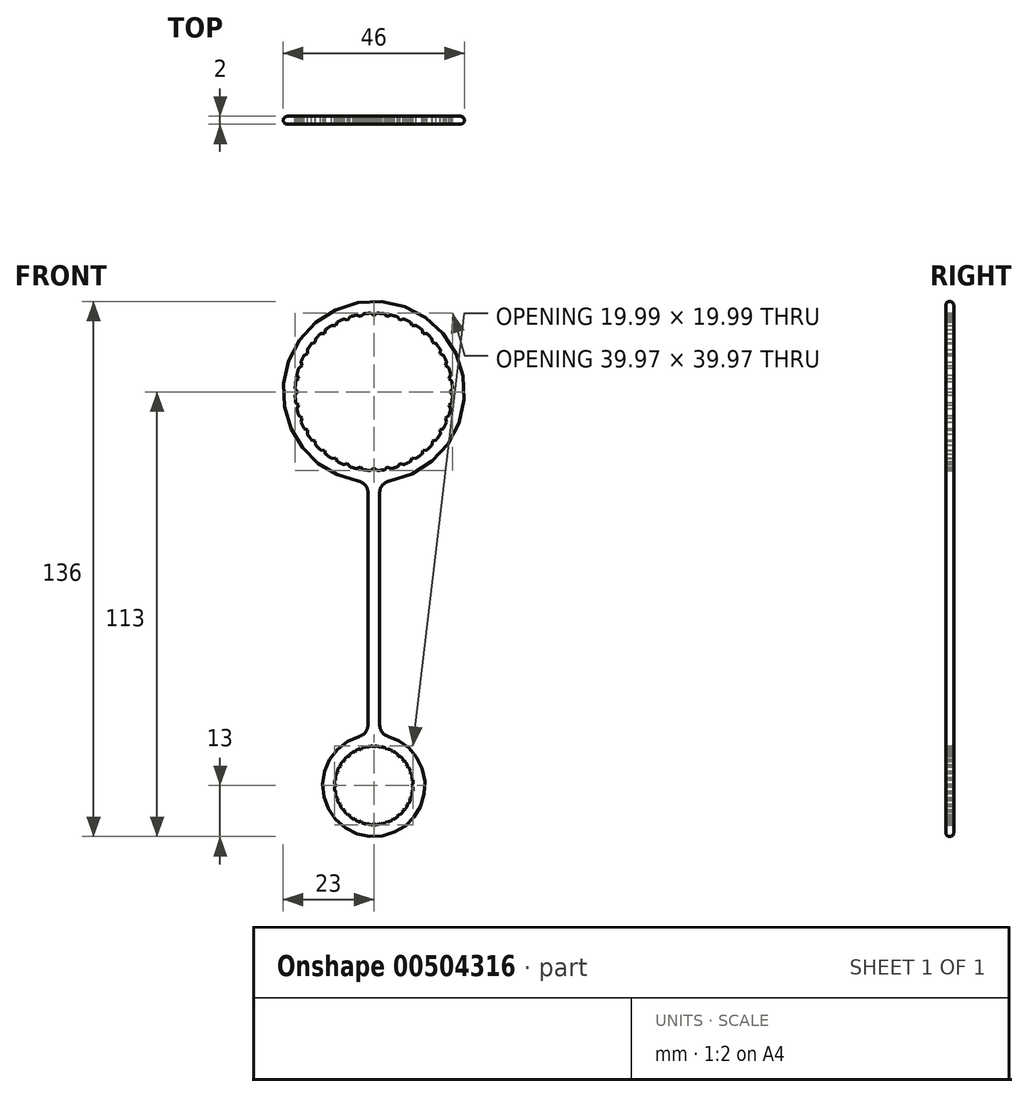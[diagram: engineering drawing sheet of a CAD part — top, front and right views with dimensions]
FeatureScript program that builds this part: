
annotation { "Feature Type Name" : "Feature", "Feature Type Description" : "" }
export const myFeature = defineFeature(function(context is Context, id is Id, definition is map)
    precondition{}
    {
        {
            var Q0;
            Q0=qCreatedBy(makeId("Front.planeOp"),FACE);
            var sketch = newSketch(context, id + "F0", { "sketchPlane" : qUnion([Q0])});
            skArc(sketch, "E0", {"start": v(6.06, 19.06) * mm, "mid": v(5.18, 19.32) * mm, "end": v(4.28, 19.54) * mm});
            skArc(sketch, "E1", {"start": v(-0.35, -90) * mm, "mid": v(-0.87, -90.04) * mm, "end": v(-1.39, -90.1) * mm});
            skPoint(sketch, "E2", {"position": v(0, -20) * mm});
            skPoint(sketch, "E3", {"position": v(0, -90) * mm});
            skArc(sketch, "E4.0", {"start": v(1.5, -22.95) * mm, "mid": v(0, 23) * mm, "end": v(-1.5, -22.95) * mm});
            skLineSegment(sketch, "E5.0", {"start": v(-1.5, -22.95) * mm, "end": v(-1.5, -87.09) * mm});
            skLineSegment(sketch, "E6.0", {"start": v(1.5, -22.95) * mm, "end": v(1.5, -87.09) * mm});
            skArc(sketch, "E7.0", {"start": v(-1.5, -87.09) * mm, "mid": v(0, -113) * mm, "end": v(1.5, -87.09) * mm});
            skPoint(sketch, "E8", {"position": v(-1.5, -22.95) * mm});
            skPoint(sketch, "E9", {"position": v(1.5, -22.95) * mm});
            skPoint(sketch, "E10", {"position": v(0, 20) * mm});
            skLineSegment(sketch, "E11", {"start": v(0, 19.41) * mm, "end": v(-0.82, 19.98) * mm});
            skLineSegment(sketch, "E12", {"start": v(0.82, 19.98) * mm, "end": v(0, 19.41) * mm});
            skLineSegment(sketch, "E13.1.0", {"start": v(4.28, 19.54) * mm, "end": v(3.37, 19.12) * mm});
            skLineSegment(sketch, "E13.1.1", {"start": v(3.37, 19.12) * mm, "end": v(2.66, 19.82) * mm});
            skLineSegment(sketch, "E13.2.0", {"start": v(7.6, 18.5) * mm, "end": v(6.64, 18.24) * mm});
            skLineSegment(sketch, "E13.2.1", {"start": v(6.64, 18.24) * mm, "end": v(6.06, 19.06) * mm});
            skLineSegment(sketch, "E13.3.0", {"start": v(10.7, 16.9) * mm, "end": v(9.7, 16.81) * mm});
            skLineSegment(sketch, "E13.3.1", {"start": v(9.7, 16.81) * mm, "end": v(9.28, 17.72) * mm});
            skLineSegment(sketch, "E13.4.0", {"start": v(13.47, 14.78) * mm, "end": v(12.48, 14.87) * mm});
            skLineSegment(sketch, "E13.4.1", {"start": v(12.48, 14.87) * mm, "end": v(12.21, 15.84) * mm});
            skLineSegment(sketch, "E13.5.0", {"start": v(15.84, 12.21) * mm, "end": v(14.87, 12.48) * mm});
            skLineSegment(sketch, "E13.5.1", {"start": v(14.87, 12.48) * mm, "end": v(14.78, 13.47) * mm});
            skLineSegment(sketch, "E13.6.0", {"start": v(17.72, 9.28) * mm, "end": v(16.81, 9.7) * mm});
            skLineSegment(sketch, "E13.6.1", {"start": v(16.81, 9.7) * mm, "end": v(16.9, 10.7) * mm});
            skLineSegment(sketch, "E13.7.0", {"start": v(19.06, 6.06) * mm, "end": v(18.24, 6.64) * mm});
            skLineSegment(sketch, "E13.7.1", {"start": v(18.24, 6.64) * mm, "end": v(18.5, 7.6) * mm});
            skLineSegment(sketch, "E13.8.0", {"start": v(19.82, 2.66) * mm, "end": v(19.12, 3.37) * mm});
            skLineSegment(sketch, "E13.8.1", {"start": v(19.12, 3.37) * mm, "end": v(19.54, 4.28) * mm});
            skLineSegment(sketch, "E13.9.0", {"start": v(19.98, -0.82) * mm, "end": v(19.41, 0) * mm});
            skLineSegment(sketch, "E13.9.1", {"start": v(19.41, 0) * mm, "end": v(19.98, 0.82) * mm});
            skLineSegment(sketch, "E13.10.0", {"start": v(19.54, -4.28) * mm, "end": v(19.12, -3.37) * mm});
            skLineSegment(sketch, "E13.10.1", {"start": v(19.12, -3.37) * mm, "end": v(19.82, -2.66) * mm});
            skLineSegment(sketch, "E13.11.0", {"start": v(18.5, -7.6) * mm, "end": v(18.24, -6.64) * mm});
            skLineSegment(sketch, "E13.11.1", {"start": v(18.24, -6.64) * mm, "end": v(19.06, -6.06) * mm});
            skLineSegment(sketch, "E13.12.0", {"start": v(16.9, -10.7) * mm, "end": v(16.81, -9.7) * mm});
            skLineSegment(sketch, "E13.12.1", {"start": v(16.81, -9.7) * mm, "end": v(17.72, -9.28) * mm});
            skLineSegment(sketch, "E13.13.0", {"start": v(14.78, -13.47) * mm, "end": v(14.87, -12.48) * mm});
            skLineSegment(sketch, "E13.13.1", {"start": v(14.87, -12.48) * mm, "end": v(15.84, -12.21) * mm});
            skLineSegment(sketch, "E13.14.0", {"start": v(12.21, -15.84) * mm, "end": v(12.48, -14.87) * mm});
            skLineSegment(sketch, "E13.14.1", {"start": v(12.48, -14.87) * mm, "end": v(13.47, -14.78) * mm});
            skLineSegment(sketch, "E13.15.0", {"start": v(9.28, -17.72) * mm, "end": v(9.7, -16.81) * mm});
            skLineSegment(sketch, "E13.15.1", {"start": v(9.7, -16.81) * mm, "end": v(10.7, -16.9) * mm});
            skLineSegment(sketch, "E13.16.0", {"start": v(6.06, -19.06) * mm, "end": v(6.64, -18.24) * mm});
            skLineSegment(sketch, "E13.16.1", {"start": v(6.64, -18.24) * mm, "end": v(7.6, -18.5) * mm});
            skLineSegment(sketch, "E13.17.0", {"start": v(2.66, -19.82) * mm, "end": v(3.37, -19.12) * mm});
            skLineSegment(sketch, "E13.17.1", {"start": v(3.37, -19.12) * mm, "end": v(4.28, -19.54) * mm});
            skLineSegment(sketch, "E13.18.0", {"start": v(-0.82, -19.98) * mm, "end": v(0, -19.41) * mm});
            skLineSegment(sketch, "E13.18.1", {"start": v(0, -19.41) * mm, "end": v(0.82, -19.98) * mm});
            skLineSegment(sketch, "E13.19.0", {"start": v(-4.28, -19.54) * mm, "end": v(-3.37, -19.12) * mm});
            skLineSegment(sketch, "E13.19.1", {"start": v(-3.37, -19.12) * mm, "end": v(-2.66, -19.82) * mm});
            skLineSegment(sketch, "E13.20.0", {"start": v(-7.6, -18.5) * mm, "end": v(-6.64, -18.24) * mm});
            skLineSegment(sketch, "E13.20.1", {"start": v(-6.64, -18.24) * mm, "end": v(-6.06, -19.06) * mm});
            skLineSegment(sketch, "E13.21.0", {"start": v(-10.7, -16.9) * mm, "end": v(-9.7, -16.81) * mm});
            skLineSegment(sketch, "E13.21.1", {"start": v(-9.7, -16.81) * mm, "end": v(-9.28, -17.72) * mm});
            skLineSegment(sketch, "E13.22.0", {"start": v(-13.47, -14.78) * mm, "end": v(-12.48, -14.87) * mm});
            skLineSegment(sketch, "E13.22.1", {"start": v(-12.48, -14.87) * mm, "end": v(-12.21, -15.84) * mm});
            skLineSegment(sketch, "E13.23.0", {"start": v(-15.84, -12.21) * mm, "end": v(-14.87, -12.48) * mm});
            skLineSegment(sketch, "E13.23.1", {"start": v(-14.87, -12.48) * mm, "end": v(-14.78, -13.47) * mm});
            skLineSegment(sketch, "E13.24.0", {"start": v(-17.72, -9.28) * mm, "end": v(-16.81, -9.7) * mm});
            skLineSegment(sketch, "E13.24.1", {"start": v(-16.81, -9.7) * mm, "end": v(-16.9, -10.7) * mm});
            skLineSegment(sketch, "E13.25.0", {"start": v(-19.06, -6.06) * mm, "end": v(-18.24, -6.64) * mm});
            skLineSegment(sketch, "E13.25.1", {"start": v(-18.24, -6.64) * mm, "end": v(-18.5, -7.6) * mm});
            skLineSegment(sketch, "E13.26.0", {"start": v(-19.82, -2.66) * mm, "end": v(-19.12, -3.37) * mm});
            skLineSegment(sketch, "E13.26.1", {"start": v(-19.12, -3.37) * mm, "end": v(-19.54, -4.28) * mm});
            skLineSegment(sketch, "E13.27.0", {"start": v(-19.98, 0.82) * mm, "end": v(-19.41, 0) * mm});
            skLineSegment(sketch, "E13.27.1", {"start": v(-19.41, 0) * mm, "end": v(-19.98, -0.82) * mm});
            skLineSegment(sketch, "E13.28.0", {"start": v(-19.54, 4.28) * mm, "end": v(-19.12, 3.37) * mm});
            skLineSegment(sketch, "E13.28.1", {"start": v(-19.12, 3.37) * mm, "end": v(-19.82, 2.66) * mm});
            skLineSegment(sketch, "E13.29.0", {"start": v(-18.5, 7.6) * mm, "end": v(-18.24, 6.64) * mm});
            skLineSegment(sketch, "E13.29.1", {"start": v(-18.24, 6.64) * mm, "end": v(-19.06, 6.06) * mm});
            skLineSegment(sketch, "E13.30.0", {"start": v(-16.9, 10.7) * mm, "end": v(-16.81, 9.7) * mm});
            skLineSegment(sketch, "E13.30.1", {"start": v(-16.81, 9.7) * mm, "end": v(-17.72, 9.28) * mm});
            skLineSegment(sketch, "E13.31.0", {"start": v(-14.78, 13.47) * mm, "end": v(-14.87, 12.48) * mm});
            skLineSegment(sketch, "E13.31.1", {"start": v(-14.87, 12.48) * mm, "end": v(-15.84, 12.21) * mm});
            skLineSegment(sketch, "E13.32.0", {"start": v(-12.21, 15.84) * mm, "end": v(-12.48, 14.87) * mm});
            skLineSegment(sketch, "E13.32.1", {"start": v(-12.48, 14.87) * mm, "end": v(-13.47, 14.78) * mm});
            skLineSegment(sketch, "E13.33.0", {"start": v(-9.28, 17.72) * mm, "end": v(-9.7, 16.81) * mm});
            skLineSegment(sketch, "E13.33.1", {"start": v(-9.7, 16.81) * mm, "end": v(-10.7, 16.9) * mm});
            skLineSegment(sketch, "E13.34.0", {"start": v(-6.06, 19.06) * mm, "end": v(-6.64, 18.24) * mm});
            skLineSegment(sketch, "E13.34.1", {"start": v(-6.64, 18.24) * mm, "end": v(-7.6, 18.5) * mm});
            skLineSegment(sketch, "E13.35.0", {"start": v(-2.66, 19.82) * mm, "end": v(-3.37, 19.12) * mm});
            skLineSegment(sketch, "E13.35.1", {"start": v(-3.37, 19.12) * mm, "end": v(-4.28, 19.54) * mm});
            skLineSegment(sketch, "E13.anchor1", {"start": v(0, 0) * mm, "end": v(-0.82, 19.98) * mm, "construction": true});
            skLineSegment(sketch, "E13.anchor2", {"start": v(0, 0) * mm, "end": v(-4.28, 19.54) * mm, "construction": true});
            skArc(sketch, "E14.trimOffspring", {"start": v(9.28, 17.72) * mm, "mid": v(8.45, 18.13) * mm, "end": v(7.6, 18.5) * mm});
            skArc(sketch, "E15.trimOffspring", {"start": v(12.21, 15.84) * mm, "mid": v(11.47, 16.38) * mm, "end": v(10.7, 16.9) * mm});
            skArc(sketch, "E16.trimOffspring", {"start": v(14.78, 13.47) * mm, "mid": v(14.14, 14.14) * mm, "end": v(13.47, 14.78) * mm});
            skArc(sketch, "E17.trimOffspring", {"start": v(16.9, 10.7) * mm, "mid": v(16.38, 11.47) * mm, "end": v(15.84, 12.21) * mm});
            skArc(sketch, "E18.trimOffspring", {"start": v(18.5, 7.6) * mm, "mid": v(18.13, 8.45) * mm, "end": v(17.72, 9.28) * mm});
            skArc(sketch, "E19.trimOffspring", {"start": v(19.54, 4.28) * mm, "mid": v(19.32, 5.18) * mm, "end": v(19.06, 6.06) * mm});
            skArc(sketch, "E20.trimOffspring", {"start": v(19.98, 0.82) * mm, "mid": v(19.92, 1.74) * mm, "end": v(19.82, 2.66) * mm});
            skArc(sketch, "E21.trimOffspring", {"start": v(19.82, -2.66) * mm, "mid": v(19.92, -1.74) * mm, "end": v(19.98, -0.82) * mm});
            skArc(sketch, "E22.trimOffspring", {"start": v(19.06, -6.06) * mm, "mid": v(19.32, -5.18) * mm, "end": v(19.54, -4.28) * mm});
            skArc(sketch, "E23.trimOffspring", {"start": v(17.72, -9.28) * mm, "mid": v(18.13, -8.45) * mm, "end": v(18.5, -7.6) * mm});
            skArc(sketch, "E24.trimOffspring", {"start": v(15.84, -12.21) * mm, "mid": v(16.38, -11.47) * mm, "end": v(16.9, -10.7) * mm});
            skArc(sketch, "E25.trimOffspring", {"start": v(13.47, -14.78) * mm, "mid": v(14.14, -14.14) * mm, "end": v(14.78, -13.47) * mm});
            skArc(sketch, "E26.trimOffspring", {"start": v(10.7, -16.9) * mm, "mid": v(11.47, -16.38) * mm, "end": v(12.21, -15.84) * mm});
            skArc(sketch, "E27.trimOffspring", {"start": v(7.6, -18.5) * mm, "mid": v(8.45, -18.13) * mm, "end": v(9.28, -17.72) * mm});
            skArc(sketch, "E28.trimOffspring", {"start": v(4.28, -19.54) * mm, "mid": v(5.18, -19.32) * mm, "end": v(6.06, -19.06) * mm});
            skArc(sketch, "E29.trimOffspring", {"start": v(0.82, -19.98) * mm, "mid": v(1.74, -19.92) * mm, "end": v(2.66, -19.82) * mm});
            skArc(sketch, "E30.trimOffspring", {"start": v(-2.66, -19.82) * mm, "mid": v(-1.74, -19.92) * mm, "end": v(-0.82, -19.98) * mm});
            skArc(sketch, "E31.trimOffspring", {"start": v(-6.06, -19.06) * mm, "mid": v(-5.18, -19.32) * mm, "end": v(-4.28, -19.54) * mm});
            skArc(sketch, "E32.trimOffspring", {"start": v(-9.28, -17.72) * mm, "mid": v(-8.45, -18.13) * mm, "end": v(-7.6, -18.5) * mm});
            skArc(sketch, "E33.trimOffspring", {"start": v(-12.21, -15.84) * mm, "mid": v(-11.47, -16.38) * mm, "end": v(-10.7, -16.9) * mm});
            skArc(sketch, "E34.trimOffspring", {"start": v(-14.78, -13.47) * mm, "mid": v(-14.14, -14.14) * mm, "end": v(-13.47, -14.78) * mm});
            skArc(sketch, "E35.trimOffspring", {"start": v(-16.9, -10.7) * mm, "mid": v(-16.38, -11.47) * mm, "end": v(-15.84, -12.21) * mm});
            skArc(sketch, "E36.trimOffspring", {"start": v(-18.5, -7.6) * mm, "mid": v(-18.13, -8.45) * mm, "end": v(-17.72, -9.28) * mm});
            skArc(sketch, "E37.trimOffspring", {"start": v(-19.54, -4.28) * mm, "mid": v(-19.32, -5.18) * mm, "end": v(-19.06, -6.06) * mm});
            skArc(sketch, "E38.trimOffspring", {"start": v(-19.98, -0.82) * mm, "mid": v(-19.92, -1.74) * mm, "end": v(-19.82, -2.66) * mm});
            skArc(sketch, "E39.trimOffspring", {"start": v(-19.82, 2.66) * mm, "mid": v(-19.92, 1.74) * mm, "end": v(-19.98, 0.82) * mm});
            skArc(sketch, "E40.trimOffspring", {"start": v(-19.06, 6.06) * mm, "mid": v(-19.32, 5.18) * mm, "end": v(-19.54, 4.28) * mm});
            skArc(sketch, "E41.trimOffspring", {"start": v(-17.72, 9.28) * mm, "mid": v(-18.13, 8.45) * mm, "end": v(-18.5, 7.6) * mm});
            skArc(sketch, "E42.trimOffspring", {"start": v(-15.84, 12.21) * mm, "mid": v(-16.38, 11.47) * mm, "end": v(-16.9, 10.7) * mm});
            skArc(sketch, "E43.trimOffspring", {"start": v(-13.47, 14.78) * mm, "mid": v(-14.14, 14.14) * mm, "end": v(-14.78, 13.47) * mm});
            skArc(sketch, "E44.trimOffspring", {"start": v(-10.7, 16.9) * mm, "mid": v(-11.47, 16.38) * mm, "end": v(-12.21, 15.84) * mm});
            skArc(sketch, "E45.trimOffspring", {"start": v(-7.6, 18.5) * mm, "mid": v(-8.45, 18.13) * mm, "end": v(-9.28, 17.72) * mm});
            skArc(sketch, "E46.trimOffspring", {"start": v(-4.28, 19.54) * mm, "mid": v(-5.18, 19.32) * mm, "end": v(-6.06, 19.06) * mm});
            skArc(sketch, "E47.trimOffspring", {"start": v(-0.82, 19.98) * mm, "mid": v(-1.74, 19.92) * mm, "end": v(-2.66, 19.82) * mm});
            skArc(sketch, "E48.trimOffspring", {"start": v(2.66, 19.82) * mm, "mid": v(1.74, 19.92) * mm, "end": v(0.82, 19.98) * mm});
            skLineSegment(sketch, "E49", {"start": v(0.35, -90) * mm, "end": v(0, -90.36) * mm});
            skLineSegment(sketch, "E50", {"start": v(0, -90.36) * mm, "end": v(-0.35, -90) * mm});
            skLineSegment(sketch, "E51.1.0", {"start": v(1.67, -90.5) * mm, "end": v(1.39, -90.1) * mm});
            skLineSegment(sketch, "E51.1.1", {"start": v(2.08, -90.22) * mm, "end": v(1.67, -90.5) * mm});
            skLineSegment(sketch, "E51.2.0", {"start": v(3.3, -90.94) * mm, "end": v(3.09, -90.49) * mm});
            skLineSegment(sketch, "E51.2.1", {"start": v(3.75, -90.73) * mm, "end": v(3.3, -90.94) * mm});
            skLineSegment(sketch, "E51.3.0", {"start": v(4.82, -91.65) * mm, "end": v(4.7, -91.17) * mm});
            skLineSegment(sketch, "E51.3.1", {"start": v(5.3, -91.52) * mm, "end": v(4.82, -91.65) * mm});
            skLineSegment(sketch, "E51.4.0", {"start": v(6.2, -92.62) * mm, "end": v(6.15, -92.12) * mm});
            skLineSegment(sketch, "E51.4.1", {"start": v(6.7, -92.57) * mm, "end": v(6.2, -92.62) * mm});
            skLineSegment(sketch, "E51.5.0", {"start": v(7.38, -93.8) * mm, "end": v(7.43, -93.3) * mm});
            skLineSegment(sketch, "E51.5.1", {"start": v(7.88, -93.85) * mm, "end": v(7.38, -93.8) * mm});
            skLineSegment(sketch, "E51.6.0", {"start": v(8.35, -95.18) * mm, "end": v(8.48, -94.7) * mm});
            skLineSegment(sketch, "E51.6.1", {"start": v(8.83, -95.3) * mm, "end": v(8.35, -95.18) * mm});
            skLineSegment(sketch, "E51.7.0", {"start": v(9.06, -96.7) * mm, "end": v(9.27, -96.25) * mm});
            skLineSegment(sketch, "E51.7.1", {"start": v(9.51, -96.91) * mm, "end": v(9.06, -96.7) * mm});
            skLineSegment(sketch, "E51.8.0", {"start": v(9.5, -98.33) * mm, "end": v(9.78, -97.92) * mm});
            skLineSegment(sketch, "E51.8.1", {"start": v(9.9, -98.61) * mm, "end": v(9.5, -98.33) * mm});
            skLineSegment(sketch, "E51.9.0", {"start": v(9.64, -100) * mm, "end": v(10, -99.65) * mm});
            skLineSegment(sketch, "E51.9.1", {"start": v(10, -100.35) * mm, "end": v(9.64, -100) * mm});
            skLineSegment(sketch, "E51.10.0", {"start": v(9.5, -101.67) * mm, "end": v(9.9, -101.39) * mm});
            skLineSegment(sketch, "E51.10.1", {"start": v(9.78, -102.08) * mm, "end": v(9.5, -101.67) * mm});
            skLineSegment(sketch, "E51.11.0", {"start": v(9.06, -103.3) * mm, "end": v(9.51, -103.09) * mm});
            skLineSegment(sketch, "E51.11.1", {"start": v(9.27, -103.75) * mm, "end": v(9.06, -103.3) * mm});
            skLineSegment(sketch, "E51.12.0", {"start": v(8.35, -104.82) * mm, "end": v(8.83, -104.7) * mm});
            skLineSegment(sketch, "E51.12.1", {"start": v(8.48, -105.3) * mm, "end": v(8.35, -104.82) * mm});
            skLineSegment(sketch, "E51.13.0", {"start": v(7.38, -106.2) * mm, "end": v(7.88, -106.15) * mm});
            skLineSegment(sketch, "E51.13.1", {"start": v(7.43, -106.7) * mm, "end": v(7.38, -106.2) * mm});
            skLineSegment(sketch, "E51.14.0", {"start": v(6.2, -107.38) * mm, "end": v(6.7, -107.43) * mm});
            skLineSegment(sketch, "E51.14.1", {"start": v(6.15, -107.88) * mm, "end": v(6.2, -107.38) * mm});
            skLineSegment(sketch, "E51.15.0", {"start": v(4.82, -108.35) * mm, "end": v(5.3, -108.48) * mm});
            skLineSegment(sketch, "E51.15.1", {"start": v(4.7, -108.83) * mm, "end": v(4.82, -108.35) * mm});
            skLineSegment(sketch, "E51.16.0", {"start": v(3.3, -109.06) * mm, "end": v(3.75, -109.27) * mm});
            skLineSegment(sketch, "E51.16.1", {"start": v(3.09, -109.51) * mm, "end": v(3.3, -109.06) * mm});
            skLineSegment(sketch, "E51.17.0", {"start": v(1.67, -109.5) * mm, "end": v(2.08, -109.78) * mm});
            skLineSegment(sketch, "E51.17.1", {"start": v(1.39, -109.9) * mm, "end": v(1.67, -109.5) * mm});
            skLineSegment(sketch, "E51.18.0", {"start": v(0, -109.64) * mm, "end": v(0.35, -110) * mm});
            skLineSegment(sketch, "E51.18.1", {"start": v(-0.35, -110) * mm, "end": v(0, -109.64) * mm});
            skLineSegment(sketch, "E51.19.0", {"start": v(-1.67, -109.5) * mm, "end": v(-1.39, -109.9) * mm});
            skLineSegment(sketch, "E51.19.1", {"start": v(-2.08, -109.78) * mm, "end": v(-1.67, -109.5) * mm});
            skLineSegment(sketch, "E51.20.0", {"start": v(-3.3, -109.06) * mm, "end": v(-3.09, -109.51) * mm});
            skLineSegment(sketch, "E51.20.1", {"start": v(-3.75, -109.27) * mm, "end": v(-3.3, -109.06) * mm});
            skLineSegment(sketch, "E51.21.0", {"start": v(-4.82, -108.35) * mm, "end": v(-4.7, -108.83) * mm});
            skLineSegment(sketch, "E51.21.1", {"start": v(-5.3, -108.48) * mm, "end": v(-4.82, -108.35) * mm});
            skLineSegment(sketch, "E51.22.0", {"start": v(-6.2, -107.38) * mm, "end": v(-6.15, -107.88) * mm});
            skLineSegment(sketch, "E51.22.1", {"start": v(-6.7, -107.43) * mm, "end": v(-6.2, -107.38) * mm});
            skLineSegment(sketch, "E51.23.0", {"start": v(-7.38, -106.2) * mm, "end": v(-7.43, -106.7) * mm});
            skLineSegment(sketch, "E51.23.1", {"start": v(-7.88, -106.15) * mm, "end": v(-7.38, -106.2) * mm});
            skLineSegment(sketch, "E51.24.0", {"start": v(-8.35, -104.82) * mm, "end": v(-8.48, -105.3) * mm});
            skLineSegment(sketch, "E51.24.1", {"start": v(-8.83, -104.7) * mm, "end": v(-8.35, -104.82) * mm});
            skLineSegment(sketch, "E51.25.0", {"start": v(-9.06, -103.3) * mm, "end": v(-9.27, -103.75) * mm});
            skLineSegment(sketch, "E51.25.1", {"start": v(-9.51, -103.09) * mm, "end": v(-9.06, -103.3) * mm});
            skLineSegment(sketch, "E51.26.0", {"start": v(-9.5, -101.67) * mm, "end": v(-9.78, -102.08) * mm});
            skLineSegment(sketch, "E51.26.1", {"start": v(-9.9, -101.39) * mm, "end": v(-9.5, -101.67) * mm});
            skLineSegment(sketch, "E51.27.0", {"start": v(-9.64, -100) * mm, "end": v(-10, -100.35) * mm});
            skLineSegment(sketch, "E51.27.1", {"start": v(-10, -99.65) * mm, "end": v(-9.64, -100) * mm});
            skLineSegment(sketch, "E51.28.0", {"start": v(-9.5, -98.33) * mm, "end": v(-9.9, -98.61) * mm});
            skLineSegment(sketch, "E51.28.1", {"start": v(-9.78, -97.92) * mm, "end": v(-9.5, -98.33) * mm});
            skLineSegment(sketch, "E51.29.0", {"start": v(-9.06, -96.7) * mm, "end": v(-9.51, -96.91) * mm});
            skLineSegment(sketch, "E51.29.1", {"start": v(-9.27, -96.25) * mm, "end": v(-9.06, -96.7) * mm});
            skLineSegment(sketch, "E51.30.0", {"start": v(-8.35, -95.18) * mm, "end": v(-8.83, -95.3) * mm});
            skLineSegment(sketch, "E51.30.1", {"start": v(-8.48, -94.7) * mm, "end": v(-8.35, -95.18) * mm});
            skLineSegment(sketch, "E51.31.0", {"start": v(-7.38, -93.8) * mm, "end": v(-7.88, -93.85) * mm});
            skLineSegment(sketch, "E51.31.1", {"start": v(-7.43, -93.3) * mm, "end": v(-7.38, -93.8) * mm});
            skLineSegment(sketch, "E51.32.0", {"start": v(-6.2, -92.62) * mm, "end": v(-6.7, -92.57) * mm});
            skLineSegment(sketch, "E51.32.1", {"start": v(-6.15, -92.12) * mm, "end": v(-6.2, -92.62) * mm});
            skLineSegment(sketch, "E51.33.0", {"start": v(-4.82, -91.65) * mm, "end": v(-5.3, -91.52) * mm});
            skLineSegment(sketch, "E51.33.1", {"start": v(-4.7, -91.17) * mm, "end": v(-4.82, -91.65) * mm});
            skLineSegment(sketch, "E51.34.0", {"start": v(-3.3, -90.94) * mm, "end": v(-3.75, -90.73) * mm});
            skLineSegment(sketch, "E51.34.1", {"start": v(-3.09, -90.49) * mm, "end": v(-3.3, -90.94) * mm});
            skLineSegment(sketch, "E51.35.0", {"start": v(-1.67, -90.5) * mm, "end": v(-2.08, -90.22) * mm});
            skLineSegment(sketch, "E51.35.1", {"start": v(-1.39, -90.1) * mm, "end": v(-1.67, -90.5) * mm});
            skLineSegment(sketch, "E51.anchor1", {"start": v(0, -100) * mm, "end": v(0, -90.36) * mm, "construction": true});
            skLineSegment(sketch, "E51.anchor2", {"start": v(0, -100) * mm, "end": v(-1.67, -90.5) * mm, "construction": true});
            skArc(sketch, "E52.trimOffspring", {"start": v(-2.08, -90.22) * mm, "mid": v(-2.59, -90.34) * mm, "end": v(-3.09, -90.49) * mm});
            skArc(sketch, "E53.trimOffspring", {"start": v(-3.75, -90.73) * mm, "mid": v(-4.23, -90.94) * mm, "end": v(-4.7, -91.17) * mm});
            skArc(sketch, "E54.trimOffspring", {"start": v(-5.3, -91.52) * mm, "mid": v(-5.74, -91.8) * mm, "end": v(-6.15, -92.12) * mm});
            skArc(sketch, "E55.trimOffspring", {"start": v(-6.7, -92.57) * mm, "mid": v(-7.07, -92.93) * mm, "end": v(-7.43, -93.3) * mm});
            skArc(sketch, "E56.trimOffspring", {"start": v(-7.88, -93.85) * mm, "mid": v(-8.2, -94.26) * mm, "end": v(-8.48, -94.7) * mm});
            skArc(sketch, "E57.trimOffspring", {"start": v(-8.83, -95.3) * mm, "mid": v(-9.06, -95.77) * mm, "end": v(-9.27, -96.25) * mm});
            skArc(sketch, "E58.trimOffspring", {"start": v(-9.51, -96.91) * mm, "mid": v(-9.66, -97.41) * mm, "end": v(-9.78, -97.92) * mm});
            skArc(sketch, "E59.trimOffspring", {"start": v(-9.9, -98.61) * mm, "mid": v(-9.96, -99.13) * mm, "end": v(-10, -99.65) * mm});
            skArc(sketch, "E60.trimOffspring", {"start": v(-10, -100.35) * mm, "mid": v(-9.96, -100.87) * mm, "end": v(-9.9, -101.39) * mm});
            skArc(sketch, "E61.trimOffspring", {"start": v(-9.78, -102.08) * mm, "mid": v(-9.66, -102.59) * mm, "end": v(-9.51, -103.09) * mm});
            skArc(sketch, "E62.trimOffspring", {"start": v(-9.27, -103.75) * mm, "mid": v(-9.06, -104.23) * mm, "end": v(-8.83, -104.7) * mm});
            skArc(sketch, "E63.trimOffspring", {"start": v(-8.48, -105.3) * mm, "mid": v(-8.2, -105.74) * mm, "end": v(-7.88, -106.15) * mm});
            skArc(sketch, "E64.trimOffspring", {"start": v(-7.43, -106.7) * mm, "mid": v(-7.07, -107.07) * mm, "end": v(-6.7, -107.43) * mm});
            skArc(sketch, "E65.trimOffspring", {"start": v(-6.15, -107.88) * mm, "mid": v(-5.74, -108.2) * mm, "end": v(-5.3, -108.48) * mm});
            skArc(sketch, "E66.trimOffspring", {"start": v(-4.7, -108.83) * mm, "mid": v(-4.23, -109.06) * mm, "end": v(-3.75, -109.27) * mm});
            skArc(sketch, "E67.trimOffspring", {"start": v(-3.09, -109.51) * mm, "mid": v(-2.59, -109.66) * mm, "end": v(-2.08, -109.78) * mm});
            skArc(sketch, "E68.trimOffspring", {"start": v(-1.39, -109.9) * mm, "mid": v(-0.87, -109.96) * mm, "end": v(-0.35, -110) * mm});
            skArc(sketch, "E69.trimOffspring", {"start": v(0.35, -110) * mm, "mid": v(0.87, -109.96) * mm, "end": v(1.39, -109.9) * mm});
            skArc(sketch, "E70.trimOffspring", {"start": v(2.08, -109.78) * mm, "mid": v(2.59, -109.66) * mm, "end": v(3.09, -109.51) * mm});
            skArc(sketch, "E71.trimOffspring", {"start": v(3.75, -109.27) * mm, "mid": v(4.23, -109.06) * mm, "end": v(4.7, -108.83) * mm});
            skArc(sketch, "E72.trimOffspring", {"start": v(5.3, -108.48) * mm, "mid": v(5.74, -108.2) * mm, "end": v(6.15, -107.88) * mm});
            skArc(sketch, "E73.trimOffspring", {"start": v(6.7, -107.43) * mm, "mid": v(7.07, -107.07) * mm, "end": v(7.43, -106.7) * mm});
            skArc(sketch, "E74.trimOffspring", {"start": v(7.88, -106.15) * mm, "mid": v(8.2, -105.74) * mm, "end": v(8.48, -105.3) * mm});
            skArc(sketch, "E75.trimOffspring", {"start": v(8.83, -104.7) * mm, "mid": v(9.06, -104.23) * mm, "end": v(9.27, -103.75) * mm});
            skArc(sketch, "E76.trimOffspring", {"start": v(9.51, -103.09) * mm, "mid": v(9.66, -102.59) * mm, "end": v(9.78, -102.08) * mm});
            skArc(sketch, "E77.trimOffspring", {"start": v(9.9, -101.39) * mm, "mid": v(9.96, -100.87) * mm, "end": v(10, -100.35) * mm});
            skArc(sketch, "E78.trimOffspring", {"start": v(10, -99.65) * mm, "mid": v(9.96, -99.13) * mm, "end": v(9.9, -98.61) * mm});
            skArc(sketch, "E79.trimOffspring", {"start": v(9.78, -97.92) * mm, "mid": v(9.66, -97.41) * mm, "end": v(9.51, -96.91) * mm});
            skArc(sketch, "E80.trimOffspring", {"start": v(9.27, -96.25) * mm, "mid": v(9.06, -95.77) * mm, "end": v(8.83, -95.3) * mm});
            skArc(sketch, "E81.trimOffspring", {"start": v(8.48, -94.7) * mm, "mid": v(8.2, -94.26) * mm, "end": v(7.88, -93.85) * mm});
            skArc(sketch, "E82.trimOffspring", {"start": v(7.43, -93.3) * mm, "mid": v(7.07, -92.93) * mm, "end": v(6.7, -92.57) * mm});
            skArc(sketch, "E83.trimOffspring", {"start": v(6.15, -92.12) * mm, "mid": v(5.74, -91.8) * mm, "end": v(5.3, -91.52) * mm});
            skArc(sketch, "E84.trimOffspring", {"start": v(4.7, -91.17) * mm, "mid": v(4.23, -90.94) * mm, "end": v(3.75, -90.73) * mm});
            skArc(sketch, "E85.trimOffspring", {"start": v(3.09, -90.49) * mm, "mid": v(2.59, -90.34) * mm, "end": v(2.08, -90.22) * mm});
            skArc(sketch, "E86.trimOffspring", {"start": v(1.39, -90.1) * mm, "mid": v(0.87, -90.04) * mm, "end": v(0.35, -90) * mm});
            skSolve(sketch);
        }
        {
            var Q0;
            Q0=makeQuery(id+"F0.imprint","IMPRINT",FACE,{"disambiguationData":[TD([[makeQuery(id+"F0.imprint","IMPRINT",EDGE,{"derivedFrom":sQuery(id+"F0.wireOp",EDGE,"E0")}),-1.0]])]});
            var Q1;
            Q1=makeQuery(id+"F0.imprint","IMPRINT",FACE,{"disambiguationData":[TD([[makeQuery(id+"F0.imprint","IMPRINT",EDGE,{"derivedFrom":sQuery(id+"F0.wireOp",EDGE,"E1")}),-1.0]])]});
            var Q2;
            Q2=sQuery(id+"F0.wireOp",EDGE,"E4.0");
            var Q3;
            Q3=sQuery(id+"F0.wireOp",EDGE,"E5.0");
            var Q4;
            Q4=sQuery(id+"F0.wireOp",EDGE,"E6.0");
            var Q5;
            Q5=sQuery(id+"F0.wireOp",EDGE,"E0");
            var Q6;
            Q6=sQuery(id+"F0.wireOp",EDGE,"E1");
            var Q7;
            Q7=sQuery(id+"F0.wireOp",EDGE,"E7.0");
            extrude(context, id + "F1", {"entities" : qUnion([Q0, Q1]), "surfaceEntities" : qUnion([Q2, Q3, Q4, Q5, Q6, Q7]), "depth" : 2 * mm});
        }
        {
            var Q0;
            Q0=makeQuery(id+"F1.opExtrude","SWEPT_EDGE",EDGE,{"disambiguationData":[OSD([sQuery(id+"F0.wireOp",EDGE,"E4.0"),sQuery(id+"F0.wireOp",EDGE,"E6.0")])]});
            var Q1;
            Q1=makeQuery(id+"F1.opExtrude","SWEPT_EDGE",EDGE,{"disambiguationData":[OSD([sQuery(id+"F0.wireOp",EDGE,"E4.0"),sQuery(id+"F0.wireOp",EDGE,"E5.0")])]});
            var Q2;
            Q2=makeQuery(id+"F1.opExtrude","SWEPT_EDGE",EDGE,{"disambiguationData":[OSD([sQuery(id+"F0.wireOp",EDGE,"E5.0"),sQuery(id+"F0.wireOp",EDGE,"E7.0")])]});
            var Q3;
            Q3=makeQuery(id+"F1.opExtrude","SWEPT_EDGE",EDGE,{"disambiguationData":[OSD([sQuery(id+"F0.wireOp",EDGE,"E6.0"),sQuery(id+"F0.wireOp",EDGE,"E7.0")])]});
            fillet(context, id + "F2", {"entities" : qUnion([Q0, Q1, Q2, Q3]), "radius" : 3 * mm, "tangentPropagation" : true, "allowEdgeOverflow" : false});
        }
        {
            var Q0;
            Q0=makeQuery(id+"F1.opExtrude","CAP_EDGE",EDGE,{"disambiguationData":[OSD([sQuery(id+"F0.wireOp",EDGE,"E4.0")])],"isStart":true});
            var Q1;
            Q1=makeQuery(id+"F1.opExtrude","CAP_EDGE",EDGE,{"disambiguationData":[OSD([sQuery(id+"F0.wireOp",EDGE,"E4.0")])],"isStart":false});
            fillet(context, id + "F3", {"entities" : qUnion([Q0, Q1]), "radius" : 1 * mm, "tangentPropagation" : true, "allowEdgeOverflow" : false});
        }
    });
